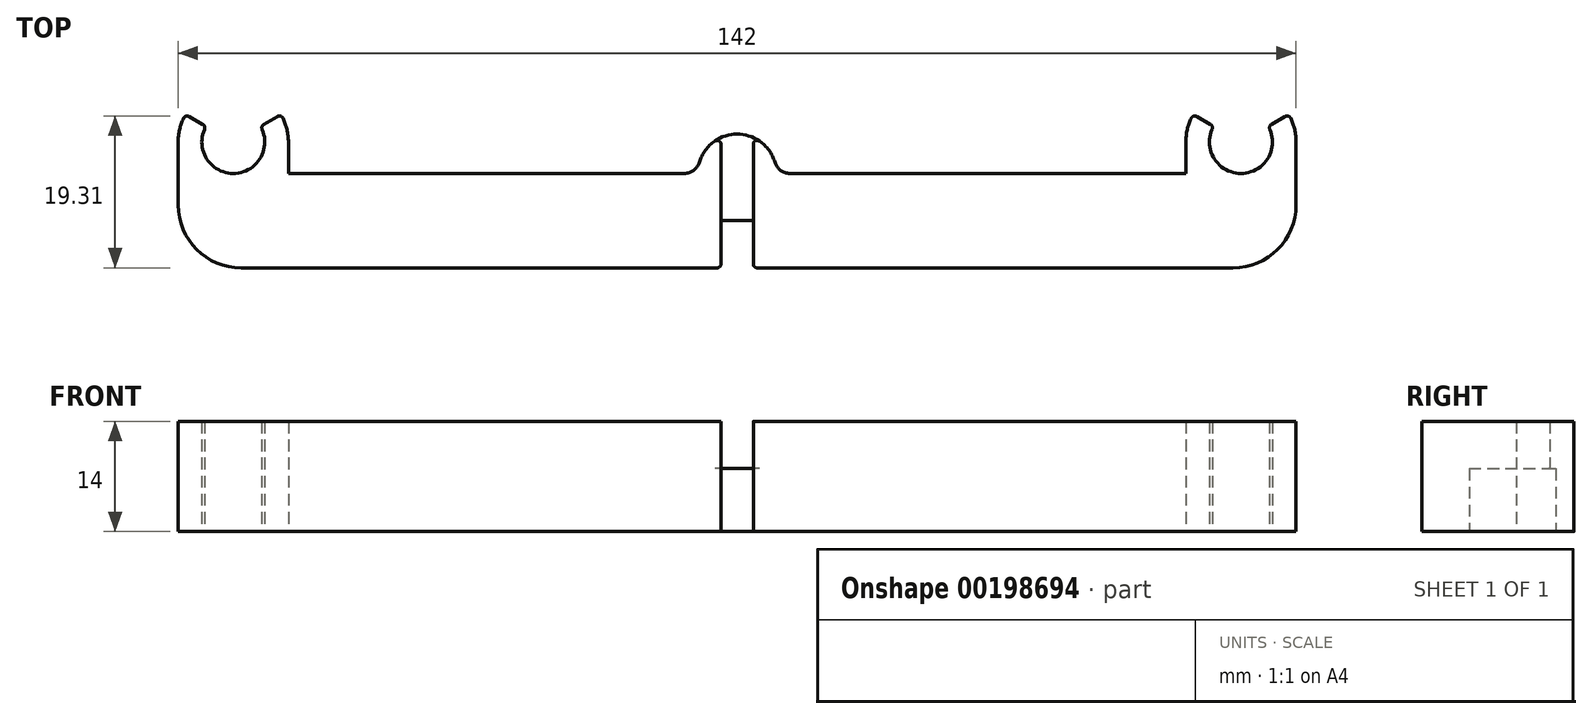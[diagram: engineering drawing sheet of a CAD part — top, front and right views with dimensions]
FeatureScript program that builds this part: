
annotation { "Feature Type Name" : "Feature", "Feature Type Description" : "" }
export const myFeature = defineFeature(function(context is Context, id is Id, definition is map)
    precondition{}
    {
        {
            var Q0;
            Q0=qCreatedBy(makeId("Top.planeOp"),FACE);
            var sketch = newSketch(context, id + "F0", { "sketchPlane" : qUnion([Q0])});
            skLineSegment(sketch, "E0", {"start": v(-2.05, -6) * mm, "end": v(-2.05, 0) * mm});
            skLineSegment(sketch, "E1", {"start": v(-2.05, 0) * mm, "end": v(0, 0) * mm});
            skLineSegment(sketch, "E2", {"start": v(0, 0) * mm, "end": v(0, 6) * mm, "construction": true});
            skLineSegment(sketch, "E3", {"start": v(0, 6) * mm, "end": v(-57, 6) * mm});
            skLineSegment(sketch, "E4", {"start": v(-71, 6) * mm, "end": v(-71, -6) * mm});
            skLineSegment(sketch, "E5", {"start": v(-71, -6) * mm, "end": v(-2.05, -6) * mm});
            skLineSegment(sketch, "E6.MirrorCS", {"start": v(0, 6) * mm, "end": v(5, 6) * mm});
            skLineSegment(sketch, "E7.MirrorCS", {"start": v(71, 6) * mm, "end": v(71, -6) * mm});
            skLineSegment(sketch, "E8.MirrorCS", {"start": v(71, -6) * mm, "end": v(2.05, -6) * mm});
            skLineSegment(sketch, "E9.MirrorCS", {"start": v(2.05, -6) * mm, "end": v(2.05, 0) * mm});
            skLineSegment(sketch, "E10.MirrorCS", {"start": v(2.05, 0) * mm, "end": v(0, 0) * mm});
            skCircle(sketch, "E11", {"center": v(-64, 10) * mm, "radius": 4 * mm, "construction": true});
            skCircle(sketch, "E12.MirrorC", {"center": v(64, 10) * mm, "radius": 4 * mm, "construction": true});
            skArc(sketch, "E13", {"start": v(-67.46, 12) * mm, "mid": v(-64, 6) * mm, "end": v(-60.54, 12) * mm});
            skArc(sketch, "E14", {"start": v(-5, 6) * mm, "mid": v(0, 11) * mm, "end": v(5, 6) * mm});
            skLineSegment(sketch, "E15", {"start": v(-67.46, 12) * mm, "end": v(-64, 10) * mm, "construction": true});
            skLineSegment(sketch, "E16", {"start": v(-64, 10) * mm, "end": v(-60.54, 12) * mm, "construction": true});
            skArc(sketch, "E17.0", {"start": v(-70.06, 13.5) * mm, "mid": v(-70.76, 11.81) * mm, "end": v(-71, 10) * mm});
            skLineSegment(sketch, "E18", {"start": v(-70.06, 13.5) * mm, "end": v(-67.46, 12) * mm});
            skLineSegment(sketch, "E19", {"start": v(-60.54, 12) * mm, "end": v(-57.94, 13.5) * mm});
            skLineSegment(sketch, "E20", {"start": v(-71, 6) * mm, "end": v(-71, 10) * mm});
            skArc(sketch, "E21.trimOffspring", {"start": v(-57, 10) * mm, "mid": v(-57.24, 11.81) * mm, "end": v(-57.94, 13.5) * mm});
            skPoint(sketch, "E22.orphan", {"position": v(71, 6) * mm});
            skArc(sketch, "E23.MirrorCS", {"start": v(67.46, 12) * mm, "mid": v(64, 6) * mm, "end": v(60.54, 12) * mm});
            skLineSegment(sketch, "E24", {"start": v(-57, 6) * mm, "end": v(-57, 10) * mm});
            skPoint(sketch, "E24.endSnap0", {"position": v(-57, 10) * mm});
            skLineSegment(sketch, "E25.MirrorCS", {"start": v(0, 6) * mm, "end": v(57, 6) * mm});
            skLineSegment(sketch, "E26.MirrorCS", {"start": v(57, 6) * mm, "end": v(57, 10) * mm});
            skArc(sketch, "E27.MirrorCS", {"start": v(57, 10) * mm, "mid": v(57.24, 11.81) * mm, "end": v(57.94, 13.5) * mm});
            skLineSegment(sketch, "E28.MirrorCS", {"start": v(60.54, 12) * mm, "end": v(57.94, 13.5) * mm});
            skLineSegment(sketch, "E29.MirrorCS", {"start": v(70.06, 13.5) * mm, "end": v(67.46, 12) * mm});
            skArc(sketch, "E30.MirrorCS", {"start": v(70.06, 13.5) * mm, "mid": v(70.76, 11.81) * mm, "end": v(71, 10) * mm});
            skLineSegment(sketch, "E31.MirrorCS", {"start": v(71, 6) * mm, "end": v(71, 10) * mm});
            skLineSegment(sketch, "E32", {"start": v(2.05, 0) * mm, "end": v(2.05, 6) * mm});
            skLineSegment(sketch, "E33", {"start": v(-2.05, 0) * mm, "end": v(-2.05, 6) * mm});
            skSolve(sketch);
        }
        {
            var Q0;
            Q0 = qSketchRegion(id + "F0", true);
            extrude(context, id + "F1", {"entities" : qUnion([Q0]), "depth" : (8 + 6) * mm});
        }
        {
            var Q0;
            Q0=makeQuery(id+"F1.opExtrude","CAP_FACE",FACE,{"disambiguationData":[OSD([sQuery(id+"F0.wireOp",EDGE,"E0"),sQuery(id+"F0.wireOp",EDGE,"E1"),sQuery(id+"F0.wireOp",EDGE,"E3"),sQuery(id+"F0.wireOp",EDGE,"E4"),sQuery(id+"F0.wireOp",EDGE,"E5"),sQuery(id+"F0.wireOp",EDGE,"E7.MirrorCS"),sQuery(id+"F0.wireOp",EDGE,"E8.MirrorCS"),sQuery(id+"F0.wireOp",EDGE,"E9.MirrorCS"),sQuery(id+"F0.wireOp",EDGE,"E10.MirrorCS"),sQuery(id+"F0.wireOp",EDGE,"E13"),sQuery(id+"F0.wireOp",EDGE,"E14"),sQuery(id+"F0.wireOp",EDGE,"E17.0"),sQuery(id+"F0.wireOp",EDGE,"E18"),sQuery(id+"F0.wireOp",EDGE,"E19"),sQuery(id+"F0.wireOp",EDGE,"E20"),sQuery(id+"F0.wireOp",EDGE,"E21.trimOffspring"),sQuery(id+"F0.wireOp",EDGE,"E23.MirrorCS"),sQuery(id+"F0.wireOp",EDGE,"E24"),sQuery(id+"F0.wireOp",EDGE,"E25.MirrorCS"),sQuery(id+"F0.wireOp",EDGE,"E26.MirrorCS"),sQuery(id+"F0.wireOp",EDGE,"E27.MirrorCS"),sQuery(id+"F0.wireOp",EDGE,"E28.MirrorCS"),sQuery(id+"F0.wireOp",EDGE,"E29.MirrorCS"),sQuery(id+"F0.wireOp",EDGE,"E30.MirrorCS"),sQuery(id+"F0.wireOp",EDGE,"E31.MirrorCS")])],"isStart":false});
            var sketch = newSketch(context, id + "F2", { "sketchPlane" : qUnion([Q0])});
            skLineSegment(sketch, "E34.bottom", {"start": v(-2.05, 0) * mm, "end": v(2.05, 0) * mm});
            skLineSegment(sketch, "E34.top", {"start": v(-2.05, 18.37) * mm, "end": v(2.05, 18.37) * mm});
            skLineSegment(sketch, "E34.left", {"start": v(-2.05, 0) * mm, "end": v(-2.05, 18.37) * mm});
            skLineSegment(sketch, "E34.right", {"start": v(2.05, 0) * mm, "end": v(2.05, 18.37) * mm});
            skSolve(sketch);
        }
        {
            var Q0;
            Q0 = qSketchRegion(id + "F2", true);
            extrude(context, id + "F3", {"entities" : qUnion([Q0]), "operationType" : NewBodyOperationType.REMOVE, "oppositeDirection" : true, "depth" : 6 * mm});
        }
        {
            var Q0;
            Q0=makeQuery(id+"F1.opExtrude","SWEPT_EDGE",EDGE,{"disambiguationData":[OSD([sQuery(id+"F0.wireOp",EDGE,"E7.MirrorCS"),sQuery(id+"F0.wireOp",EDGE,"E8.MirrorCS")])]});
            var Q1;
            Q1=makeQuery(id+"F1.opExtrude","SWEPT_EDGE",EDGE,{"disambiguationData":[OSD([sQuery(id+"F0.wireOp",EDGE,"E4"),sQuery(id+"F0.wireOp",EDGE,"E5")])]});
            fillet(context, id + "F4", {"entities" : qUnion([Q0, Q1]), "radius" : 8 * mm, "allowEdgeOverflow" : false});
        }
        {
            var Q0;
            Q0=makeQuery(id+"F1.opExtrude","SWEPT_EDGE",EDGE,{"disambiguationData":[OSD([sQuery(id+"F0.wireOp",EDGE,"E8.MirrorCS"),sQuery(id+"F0.wireOp",EDGE,"E9.MirrorCS")])]});
            var Q1;
            Q1=makeQuery(id+"F1.opExtrude","SWEPT_EDGE",EDGE,{"disambiguationData":[OSD([sQuery(id+"F0.wireOp",EDGE,"E0"),sQuery(id+"F0.wireOp",EDGE,"E5")])]});
            var Q2;
            Q2=makeQuery(id+"F3.boolean.opBoolean","INTERSECT",EDGE,{"derivedFrom":[makeQuery(id+"F1.opExtrude","SWEPT_FACE",FACE,{"disambiguationData":[OSD([sQuery(id+"F0.wireOp",EDGE,"E14")])]}),makeQuery(id+"F3.opExtrude","SWEPT_FACE",FACE,{"disambiguationData":[OSD([sQuery(id+"F2.wireOp",EDGE,"E34.left")])]})]});
            var Q3;
            Q3=makeQuery(id+"F3.boolean.opBoolean","INTERSECT",EDGE,{"derivedFrom":[makeQuery(id+"F1.opExtrude","SWEPT_FACE",FACE,{"disambiguationData":[OSD([sQuery(id+"F0.wireOp",EDGE,"E14")])]}),makeQuery(id+"F3.opExtrude","SWEPT_FACE",FACE,{"disambiguationData":[OSD([sQuery(id+"F2.wireOp",EDGE,"E34.right")])]})]});
            var Q4;
            Q4=makeQuery(id+"F1.opExtrude","SWEPT_EDGE",EDGE,{"disambiguationData":[OSD([sQuery(id+"F0.wireOp",EDGE,"E13"),sQuery(id+"F0.wireOp",EDGE,"E18")])]});
            var Q5;
            Q5=makeQuery(id+"F1.opExtrude","SWEPT_EDGE",EDGE,{"disambiguationData":[OSD([sQuery(id+"F0.wireOp",EDGE,"E13"),sQuery(id+"F0.wireOp",EDGE,"E19")])]});
            var Q6;
            Q6=makeQuery(id+"F1.opExtrude","SWEPT_EDGE",EDGE,{"disambiguationData":[OSD([sQuery(id+"F0.wireOp",EDGE,"E23.MirrorCS"),sQuery(id+"F0.wireOp",EDGE,"E28.MirrorCS")])]});
            var Q7;
            Q7=makeQuery(id+"F1.opExtrude","SWEPT_EDGE",EDGE,{"disambiguationData":[OSD([sQuery(id+"F0.wireOp",EDGE,"E23.MirrorCS"),sQuery(id+"F0.wireOp",EDGE,"E29.MirrorCS")])]});
            var Q8;
            Q8=makeQuery(id+"F1.opExtrude","SWEPT_EDGE",EDGE,{"disambiguationData":[OSD([sQuery(id+"F0.wireOp",EDGE,"E29.MirrorCS"),sQuery(id+"F0.wireOp",EDGE,"E30.MirrorCS")])]});
            var Q9;
            Q9=makeQuery(id+"F1.opExtrude","SWEPT_EDGE",EDGE,{"disambiguationData":[OSD([sQuery(id+"F0.wireOp",EDGE,"E27.MirrorCS"),sQuery(id+"F0.wireOp",EDGE,"E28.MirrorCS")])]});
            var Q10;
            Q10=makeQuery(id+"F1.opExtrude","SWEPT_EDGE",EDGE,{"disambiguationData":[OSD([sQuery(id+"F0.wireOp",EDGE,"E19"),sQuery(id+"F0.wireOp",EDGE,"E21.trimOffspring")])]});
            var Q11;
            Q11=makeQuery(id+"F1.opExtrude","SWEPT_EDGE",EDGE,{"disambiguationData":[OSD([sQuery(id+"F0.wireOp",EDGE,"E17.0"),sQuery(id+"F0.wireOp",EDGE,"E18")])]});
            fillet(context, id + "F5", {"entities" : qUnion([Q0, Q1, Q2, Q3, Q4, Q5, Q6, Q7, Q8, Q9, Q10, Q11]), "radius" : 0.5 * mm, "allowEdgeOverflow" : false});
        }
        {
            var Q0;
            Q0=makeQuery(id+"F1.opExtrude","SWEPT_EDGE",EDGE,{"disambiguationData":[OSD([sQuery(id+"F0.wireOp",EDGE,"E3"),sQuery(id+"F0.wireOp",EDGE,"E14")])]});
            var Q1;
            Q1=makeQuery(id+"F1.opExtrude","SWEPT_EDGE",EDGE,{"disambiguationData":[OSD([sQuery(id+"F0.wireOp",EDGE,"E14"),sQuery(id+"F0.wireOp",EDGE,"E25.MirrorCS")])]});
            fillet(context, id + "F6", {"entities" : qUnion([Q0, Q1]), "radius" : 2 * mm, "allowEdgeOverflow" : false});
        }
    });
